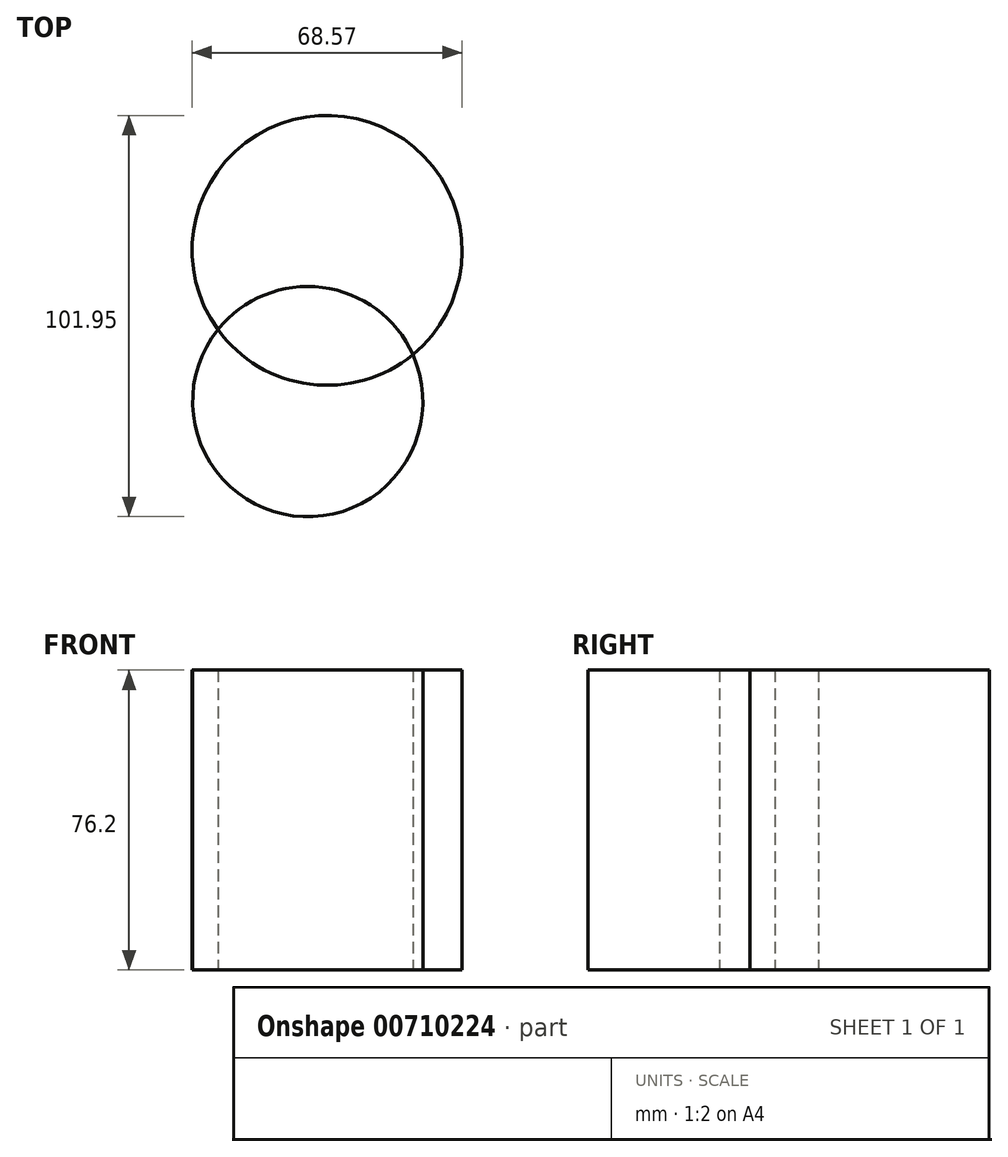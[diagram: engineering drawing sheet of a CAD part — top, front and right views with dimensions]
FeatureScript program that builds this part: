
annotation { "Feature Type Name" : "Feature", "Feature Type Description" : "" }
export const myFeature = defineFeature(function(context is Context, id is Id, definition is map)
    precondition{}
    {
        {
            var Q0;
            Q0=qCreatedBy(makeId("Top.planeOp"),FACE);
            var sketch = newSketch(context, id + "F0", { "sketchPlane" : qUnion([Q0])});
            skCircle(sketch, "E0", {"center": v(-19.93, 45.17) * mm, "radius": 34.29 * mm});
            skCircle(sketch, "E1", {"center": v(-24.83, 6.74) * mm, "radius": 29.25 * mm});
            skSolve(sketch);
        }
        {
            var Q0;
            {var subQ0=sQuery(id+"F0.wireOp",EDGE,"E1");var subQ1=sQuery(id+"F0.wireOp",EDGE,"E0");var subQ2=makeQuery(id+"F0.imprint","INTERSECT",VERTEX,{"disambiguationData":[OD(0.0)],"derivedFrom":[subQ1,subQ0]});Q0=makeQuery(id+"F0.imprint","IMPRINT",FACE,{"disambiguationData":[TD([[makeQuery(id+"F0.imprint","IMPRINT",EDGE,{"disambiguationData":[TD([[subQ2,1.0]])],"derivedFrom":subQ1}),1.0]])]});}
            var Q1;
            {var subQ0=sQuery(id+"F0.wireOp",EDGE,"E1");var subQ1=sQuery(id+"F0.wireOp",EDGE,"E0");var subQ2=makeQuery(id+"F0.imprint","INTERSECT",VERTEX,{"disambiguationData":[OD(0.0)],"derivedFrom":[subQ1,subQ0]});Q1=makeQuery(id+"F0.imprint","IMPRINT",FACE,{"disambiguationData":[TD([[makeQuery(id+"F0.imprint","IMPRINT",EDGE,{"disambiguationData":[TD([[subQ2,-1.0]])],"derivedFrom":subQ1}),-1.0]])]});}
            extrude(context, id + "F1", {"entities" : qUnion([Q0, Q1]), "depth" : 76.2 * mm, "offsetDistance" : 25.4 * mm});
        }
    });
